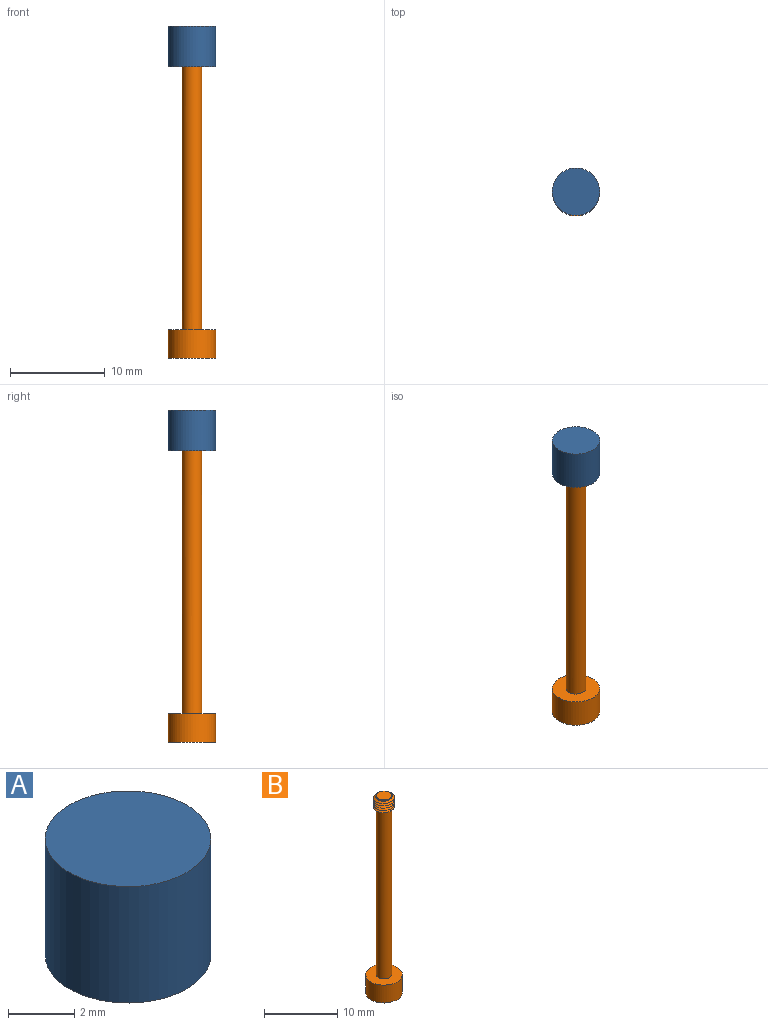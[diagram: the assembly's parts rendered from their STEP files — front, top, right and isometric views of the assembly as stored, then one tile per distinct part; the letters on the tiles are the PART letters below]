
ASSEMBLY  parts=2 mates=1
PART A: 10 faces, bbox 5x5x4.3 mm
  f0: cylinder r=1.2mm len=2.4mm, axis (0,0,-1), area 2mm2, adj f2,f3,f5,f7,f8
  f1: cylinder r=2.5mm len=5mm, axis (0,0,-1), area 67.5mm2, adj f2,f4
  f2: plane 5x5mm, normal (0,0,-1), area 15.1mm2, adj f0,f1
  f3: plane 2.4x2.4mm, normal (0,0,-1), area 4.5mm2, adj f0,f9
  f4: plane 5x5mm, normal (0,0,1), area 19.6mm2, adj f1
  f5: plane 0.45x0.39mm, normal (0,1,0), area 0.1mm2, adj f0,f7,f8
  f6: plane 0.45x0.39mm, normal (0,-1,0), area 0.1mm2, adj f7,f8,f9
  f7: bspline ~3.67x3.18mm, area 19.7mm2, adj f0,f5,f6,f8,f9
  f8: bspline ~3.67x3.18mm, area 19.7mm2, adj f0,f5,f6,f7
  f9: cylinder r=1.2mm len=2.4mm, axis (0,0,1), area 1.7mm2, adj f3,f6,f7
PART B: 12 faces, bbox 5x5x33 mm
  f0: cylinder r=1.05mm len=28.05mm, axis (0,0,-1), area 183.8mm2, adj f3,f5,f7
  f1: cylinder r=2.5mm len=5mm, axis (0,0,1), area 47.1mm2, adj f2,f3
  f2: plane 5x5mm, normal (0,0,-1), area 19.6mm2, adj f1
  f3: plane 5x5mm, normal (0,0,1), area 16.2mm2, adj f0,f1
  f4: plane 0.41x0.39mm, normal (0,1,0), area 0.1mm2, adj f6,f8,f9,f11
  f5: plane 0.41x0.39mm, normal (0,-1,0), area 0.1mm2, adj f0,f7,f8,f9
  f6: bspline ~2.23x2.23mm, area 0.5mm2, adj f4,f9,f11
  f7: bspline ~2.58x2.23mm, area 0.5mm2, adj f0,f5,f8
  f8: bspline ~3.33x2.88mm, area 15mm2, adj f4,f5,f7,f9
  f9: bspline ~3.33x2.88mm, area 15.1mm2, adj f4,f5,f6,f8
  f10: plane 2.1x2.1mm, normal (0,0,1), area 3.5mm2, adj f11
  f11: cylinder r=1.05mm len=2.1mm, axis (0,0,-1), area 1.2mm2, adj f4,f6,f10
PLACE A rot(axis=(0,0,1),180deg) t=(-11.2,-7.03,27.02)mm
PLACE B t=(-8.52,8.44,-0.68)mm
MATE revolute A.f0 <-> B.f0  axis (0,0,-1) through (-8.52,8.44,29.32)mm
